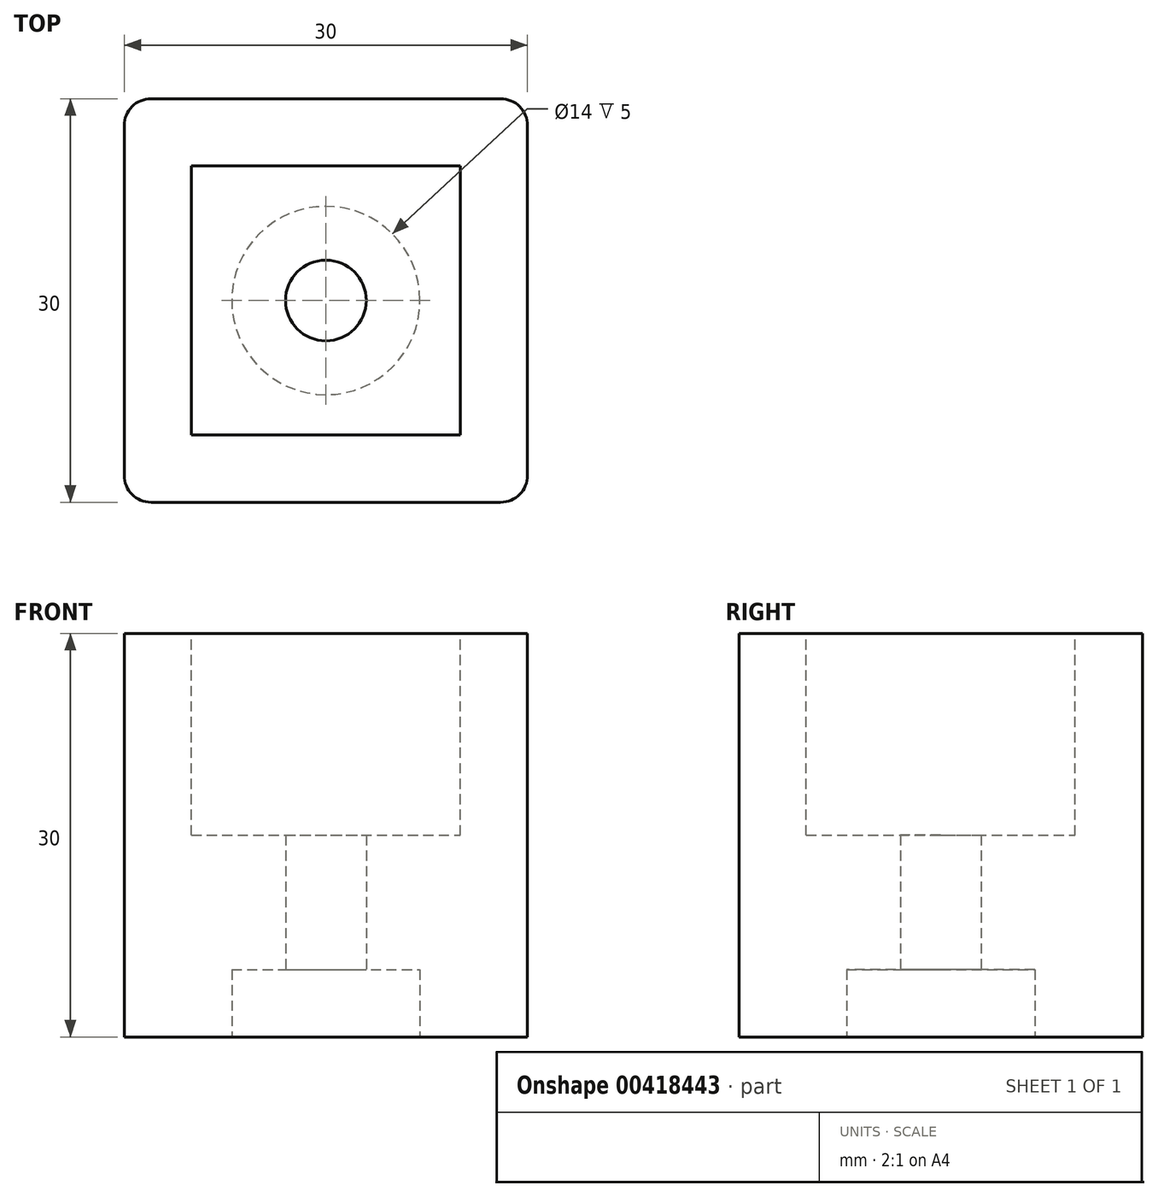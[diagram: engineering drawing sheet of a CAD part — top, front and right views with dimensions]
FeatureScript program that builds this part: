
annotation { "Feature Type Name" : "Feature", "Feature Type Description" : "" }
export const myFeature = defineFeature(function(context is Context, id is Id, definition is map)
    precondition{}
    {
        {
            var Q0;
            Q0=qCreatedBy(makeId("Top.planeOp"),FACE);
            var sketch = newSketch(context, id + "F0", { "sketchPlane" : qUnion([Q0])});
            skLineSegment(sketch, "E0.bottom", {"start": v(0, 0) * mm, "end": v(30, 0) * mm});
            skLineSegment(sketch, "E0.top", {"start": v(0, 30) * mm, "end": v(30, 30) * mm});
            skLineSegment(sketch, "E0.left", {"start": v(0, 0) * mm, "end": v(0, 30) * mm});
            skLineSegment(sketch, "E0.right", {"start": v(30, 0) * mm, "end": v(30, 30) * mm});
            skSolve(sketch);
        }
        {
            var Q0;
            Q0 = qSketchRegion(id + "F0", true);
            extrude(context, id + "F1", {"entities" : qUnion([Q0]), "depth" : 30 * mm, "offsetDistance" : 25 * mm});
        }
        {
            var Q0;
            Q0=makeQuery(id+"F1.opExtrude","CAP_FACE",FACE,{"disambiguationData":[OSD([sQuery(id+"F0.wireOp",EDGE,"E0.bottom"),sQuery(id+"F0.wireOp",EDGE,"E0.top"),sQuery(id+"F0.wireOp",EDGE,"E0.left"),sQuery(id+"F0.wireOp",EDGE,"E0.right")])],"isStart":false});
            var sketch = newSketch(context, id + "F2", { "sketchPlane" : qUnion([Q0])});
            skLineSegment(sketch, "E1.bottom", {"start": v(5, 5) * mm, "end": v(25, 5) * mm});
            skLineSegment(sketch, "E1.top", {"start": v(5, 25) * mm, "end": v(25, 25) * mm});
            skLineSegment(sketch, "E1.left", {"start": v(5, 5) * mm, "end": v(5, 25) * mm});
            skLineSegment(sketch, "E1.right", {"start": v(25, 5) * mm, "end": v(25, 25) * mm});
            skSolve(sketch);
        }
        {
            var Q0;
            Q0 = qSketchRegion(id + "F2", true);
            extrude(context, id + "F3", {"entities" : qUnion([Q0]), "operationType" : NewBodyOperationType.REMOVE, "oppositeDirection" : true, "depth" : 15 * mm, "offsetDistance" : 25 * mm});
        }
        {
            var Q0;
            Q0=makeQuery(id+"F1.opExtrude","CAP_FACE",FACE,{"disambiguationData":[OSD([sQuery(id+"F0.wireOp",EDGE,"E0.bottom"),sQuery(id+"F0.wireOp",EDGE,"E0.top"),sQuery(id+"F0.wireOp",EDGE,"E0.left"),sQuery(id+"F0.wireOp",EDGE,"E0.right")])],"isStart":true});
            var sketch = newSketch(context, id + "F4", { "sketchPlane" : qUnion([Q0])});
            skCircle(sketch, "E2", {"center": v(15, -15) * mm, "radius": 3 * mm});
            skSolve(sketch);
        }
        {
            var Q0;
            Q0 = qSketchRegion(id + "F4", true);
            extrude(context, id + "F5", {"entities" : qUnion([Q0]), "operationType" : NewBodyOperationType.REMOVE, "oppositeDirection" : true, "depth" : 25 * mm, "offsetDistance" : 25 * mm});
        }
        {
            var Q0;
            Q0=makeQuery(id+"F1.opExtrude","CAP_FACE",FACE,{"disambiguationData":[OSD([sQuery(id+"F0.wireOp",EDGE,"E0.bottom"),sQuery(id+"F0.wireOp",EDGE,"E0.top"),sQuery(id+"F0.wireOp",EDGE,"E0.left"),sQuery(id+"F0.wireOp",EDGE,"E0.right")])],"isStart":true});
            var sketch = newSketch(context, id + "F6", { "sketchPlane" : qUnion([Q0])});
            skCircle(sketch, "E3", {"center": v(15, -15) * mm, "radius": 7 * mm});
            skSolve(sketch);
        }
        {
            var Q0;
            Q0 = qSketchRegion(id + "F6", true);
            extrude(context, id + "F7", {"entities" : qUnion([Q0]), "operationType" : NewBodyOperationType.REMOVE, "oppositeDirection" : true, "depth" : 5 * mm, "offsetDistance" : 25 * mm});
        }
        {
            var Q0;
            Q0=makeQuery(id+"F3.boolean.opBoolean","COPY",EDGE,{"derivedFrom":makeQuery(id+"F3.opExtrude","CAP_EDGE",EDGE,{"disambiguationData":[OSD([sQuery(id+"F2.wireOp",EDGE,"E1.left")])],"isStart":true})});
            var Q1;
            Q1=makeQuery(id+"F3.boolean.opBoolean","COPY",EDGE,{"derivedFrom":makeQuery(id+"F3.opExtrude","CAP_EDGE",EDGE,{"disambiguationData":[OSD([sQuery(id+"F2.wireOp",EDGE,"E1.top")])],"isStart":true})});
            var Q2;
            Q2=makeQuery(id+"F3.boolean.opBoolean","COPY",EDGE,{"derivedFrom":makeQuery(id+"F3.opExtrude","CAP_EDGE",EDGE,{"disambiguationData":[OSD([sQuery(id+"F2.wireOp",EDGE,"E1.right")])],"isStart":true})});
            var Q3;
            Q3=makeQuery(id+"F3.boolean.opBoolean","COPY",EDGE,{"derivedFrom":makeQuery(id+"F3.opExtrude","CAP_EDGE",EDGE,{"disambiguationData":[OSD([sQuery(id+"F2.wireOp",EDGE,"E1.bottom")])],"isStart":true})});
            var Q4;
            Q4=makeQuery(id+"F1.opExtrude","SWEPT_EDGE",EDGE,{"disambiguationData":[OSD([sQuery(id+"F0.wireOp",EDGE,"E0.bottom"),sQuery(id+"F0.wireOp",EDGE,"E0.right")])]});
            var Q5;
            Q5=makeQuery(id+"F1.opExtrude","SWEPT_EDGE",EDGE,{"disambiguationData":[OSD([sQuery(id+"F0.wireOp",EDGE,"E0.top"),sQuery(id+"F0.wireOp",EDGE,"E0.right")])]});
            var Q6;
            Q6=makeQuery(id+"F1.opExtrude","SWEPT_EDGE",EDGE,{"disambiguationData":[OSD([sQuery(id+"F0.wireOp",EDGE,"E0.bottom"),sQuery(id+"F0.wireOp",EDGE,"E0.left")])]});
            var Q7;
            Q7=makeQuery(id+"F1.opExtrude","SWEPT_EDGE",EDGE,{"disambiguationData":[OSD([sQuery(id+"F0.wireOp",EDGE,"E0.top"),sQuery(id+"F0.wireOp",EDGE,"E0.left")])]});
            fillet(context, id + "F8", {"entities" : qUnion([Q0, Q1, Q2, Q3, Q4, Q5, Q6, Q7]), "radius" : 2 * mm, "tangentPropagation" : true, "allowEdgeOverflow" : false});
        }
    });
